# Revit family: Maxlogic ПДУ “Пуск пожаротушения”
name_source: partatom
category: Fire Alarm Devices
units: mm (PartAtom-declared; Revit-internal decimal feet)

## family parameters
Cut with Voids When Loaded = No
Host = Face
Maintain Annotation Orientation = Yes
OmniClass Number = 23.85.30.21
OmniClass Title = Environmental Detection/Registration
Part Type = Normal
Room Calculation Point = No
Round Connector Dimension = Use Diameter
Shared = No

## types (1)
- Maxlogic ПДУ “Пуск пожаротушения”
    Cost = 0 $
    Default Elevation = 0 mm  [stored 0 ft]
    Description = ПДУ “Пуск пожаротушения”
    Manufacturer = Mavili Elektronik Ticaret A.Ş.
    Model = MaxLogic
    URL = https://www.mavili.com.tr
    Адрес №1 = Şerifali Mahallesi Kutup Sokak No:27/1-2-4 Ümraniye TR-34775 İSTANBUL
    Вес = 140 гр
    Вторичный материал = Пластмассовый
    Гарантийный срок = Года
    Гарантийный срок запчастей = 2
    Гарантия срока службы = 2
    Главный Материал = Желтый пластмассовый ABS
    Диапазон рабочего напряжения = 10-30 В Пост. ток
    Инструкция по установке = https://mavilielektronik.com
    Класс защиты = IP22D
    Код продукта = ML-2710.MR
    Монтажная высота = Выше пола на 140 см (+/-200мм)
    Монтажная поверхность = Настенная
    Номер позы общественных работ = 833-260
    Номер телефона = (+)90 216 466 45 05
    Номер факса = (+)90 216 466 45 10
    Номинальная высота = 91 мм
    Номинальная глубина = 58 мм
    Номинальная ширина = 87 мм
    Прозрачная защитная крышка = ML-0710
    Производительность кода = EN 12094-3
    Рабочая Температура = (-10°C) - (+55°C)
    Рабочее напряжение (по умолчанию) = 24 В Пост. ток
    Цвет = Желтый

note: [stored X ft] marks values corroborated as IEEE doubles in the binary element streams (Revit-internal decimal feet)

## geometry (parser evidence)
native form markers: Sweep x3
no freeform markers — native parametric forms only
